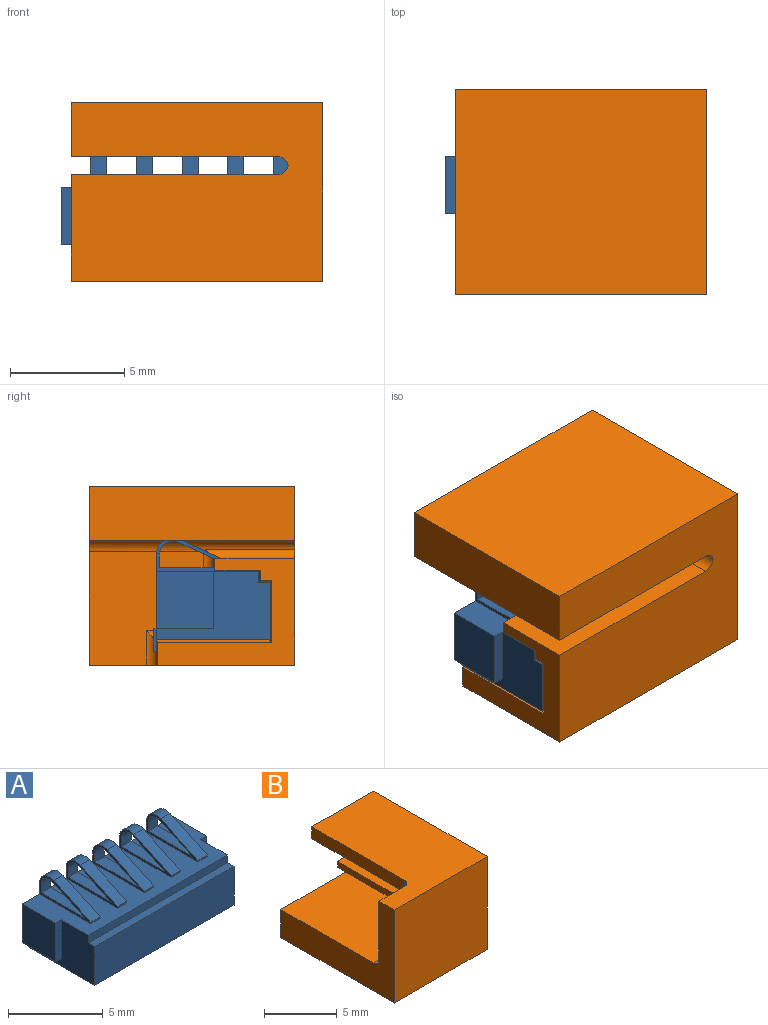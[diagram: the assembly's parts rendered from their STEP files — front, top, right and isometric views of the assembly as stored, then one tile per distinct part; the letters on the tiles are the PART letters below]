
ASSEMBLY  parts=2 mates=1
PART A: 89 faces, bbox 11.3x5.1x5 mm
  f0: plane 11.3x4.5mm, normal (0,0,1), area 35.6mm2, adj f1,f2,f4,f5,f6,f8,f9,f11
  f1: plane 2.5x2.5mm, normal (-1,0,0), area 6.2mm2, adj f0,f4,f5,f12
  f2: plane 2.5x2.5mm, normal (1,0,0), area 6.2mm2, adj f0,f4,f9,f13
  f3: plane 10.4x5mm, normal (0,0,-1), area 52mm2, adj f4,f6,f7,f8,f14,f20,f26,f32
  f4: plane 11.3x3.72mm, normal (0,1,0), area 34.2mm2, adj f0,f1,f2,f3,f6,f8,f12,f13
  f5: plane 2.5x0.45mm, normal (0,-1,0), area 1.1mm2, adj f0,f1,f6,f12
  f6: plane 5x3mm, normal (-1,0,0), area 8.5mm2, adj f0,f3,f4,f5,f7,f10,f11,f12
  f7: plane 10.4x2.5mm, normal (0,-1,0), area 26mm2, adj f3,f6,f8,f10
  f8: plane 5x3mm, normal (1,0,0), area 8.5mm2, adj f0,f3,f4,f7,f9,f10,f11,f13
  f9: plane 2.5x0.45mm, normal (0,-1,0), area 1.1mm2, adj f0,f2,f8,f13
  f10: plane 10.4x0.5mm, normal (0,0,1), area 5.2mm2, adj f6,f7,f8,f11
  f11: plane 10.4x0.5mm, normal (0,-1,0), area 5.2mm2, adj f0,f6,f8,f10
  f12: plane 2.5x0.45mm, normal (0,0,-1), area 1.1mm2, adj f1,f4,f5,f6
  f13: plane 2.5x0.45mm, normal (0,0,-1), area 1.1mm2, adj f2,f4,f8,f9
  f14: plane 0.7x0.5mm, normal (0,-1,0), area 0.4mm2, adj f3,f15,f16,f18
  f15: plane 1x0.13mm, normal (1,0,0), area 0.1mm2, adj f4,f14,f17,f18,f19
  f16: plane 1x0.13mm, normal (-1,0,0), area 0.1mm2, adj f4,f14,f17,f18,f19
  f17: plane 1x0.7mm, normal (0,1,0), area 0.7mm2, adj f15,f16,f18,f19
  f18: plane 0.7x0.13mm, normal (0,0,-1), area 0.1mm2, adj f14,f15,f16,f17
  f19: plane 0.7x0.13mm, normal (0,0,1), area 0.1mm2, adj f4,f15,f16,f17
  f20: plane 0.7x0.5mm, normal (0,-1,0), area 0.4mm2, adj f3,f21,f23,f24
  f21: plane 1x0.13mm, normal (-1,0,0), area 0.1mm2, adj f4,f20,f22,f24,f25
  f22: plane 1x0.7mm, normal (0,1,0), area 0.7mm2, adj f21,f23,f24,f25
  f23: plane 1x0.13mm, normal (1,0,0), area 0.1mm2, adj f4,f20,f22,f24,f25
  f24: plane 0.7x0.13mm, normal (0,0,-1), area 0.1mm2, adj f20,f21,f22,f23
  f25: plane 0.7x0.13mm, normal (0,0,1), area 0.1mm2, adj f4,f21,f22,f23
  f26: plane 0.7x0.5mm, normal (0,-1,0), area 0.4mm2, adj f3,f27,f29,f30
  f27: plane 1x0.13mm, normal (-1,0,0), area 0.1mm2, adj f4,f26,f28,f30,f31
  f28: plane 1x0.7mm, normal (0,1,0), area 0.7mm2, adj f27,f29,f30,f31
  f29: plane 1x0.13mm, normal (1,0,0), area 0.1mm2, adj f4,f26,f28,f30,f31
  f30: plane 0.7x0.13mm, normal (0,0,-1), area 0.1mm2, adj f26,f27,f28,f29
  f31: plane 0.7x0.13mm, normal (0,0,1), area 0.1mm2, adj f4,f27,f28,f29
  f32: plane 0.7x0.5mm, normal (0,-1,0), area 0.4mm2, adj f3,f33,f35,f36
  f33: plane 1x0.13mm, normal (-1,0,0), area 0.1mm2, adj f4,f32,f34,f36,f37
  f34: plane 1x0.7mm, normal (0,1,0), area 0.7mm2, adj f33,f35,f36,f37
  f35: plane 1x0.13mm, normal (1,0,0), area 0.1mm2, adj f4,f32,f34,f36,f37
  f36: plane 0.7x0.13mm, normal (0,0,-1), area 0.1mm2, adj f32,f33,f34,f35
  f37: plane 0.7x0.13mm, normal (0,0,1), area 0.1mm2, adj f4,f33,f34,f35
  f38: plane 0.7x0.5mm, normal (0,-1,0), area 0.3mm2, adj f3,f39,f41,f42
  f39: plane 1x0.13mm, normal (-1,0,0), area 0.1mm2, adj f4,f38,f40,f42,f43
  f40: plane 1x0.7mm, normal (0,1,0), area 0.7mm2, adj f39,f41,f42,f43
  f41: plane 1x0.13mm, normal (1,0,0), area 0.1mm2, adj f4,f38,f40,f42,f43
  f42: plane 0.7x0.13mm, normal (0,0,-1), area 0.1mm2, adj f38,f39,f40,f41
  f43: plane 0.7x0.13mm, normal (0,0,1), area 0.1mm2, adj f4,f39,f40,f41
  f44: plane 3.85x1.47mm, normal (-1,0,0), area 1.3mm2, adj f0,f4,f45,f47,f68,f85,f86,f87
  f45: plane 0.7x0.1mm, normal (0,-1,0), area 0.1mm2, adj f0,f44,f46,f47
  f46: plane 3.85x1.47mm, normal (1,0,0), area 1.3mm2, adj f0,f4,f45,f47,f68,f85,f86,f87
  f47: plane 2.78x1.3mm, normal (0,-0.42,0.91), area 2.1mm2, adj f44,f45,f46,f68
  f48: plane 3.85x1.47mm, normal (-1,0,0), area 1.3mm2, adj f0,f4,f49,f51,f67,f81,f82,f83
  f49: plane 0.7x0.1mm, normal (0,-1,0), area 0.1mm2, adj f0,f48,f50,f51
  f50: plane 3.85x1.47mm, normal (1,0,0), area 1.3mm2, adj f0,f4,f49,f51,f67,f81,f82,f83
  f51: plane 2.78x1.3mm, normal (0,-0.42,0.91), area 2.1mm2, adj f48,f49,f50,f67
  f52: plane 3.85x1.47mm, normal (-1,0,0), area 1.3mm2, adj f0,f4,f53,f55,f66,f77,f78,f79
  f53: plane 0.7x0.1mm, normal (0,-1,0), area 0.1mm2, adj f0,f52,f54,f55
  f54: plane 3.85x1.47mm, normal (1,0,0), area 1.3mm2, adj f0,f4,f53,f55,f66,f77,f78,f79
  f55: plane 2.78x1.3mm, normal (0,-0.42,0.91), area 2.1mm2, adj f52,f53,f54,f66
  f56: plane 3.85x1.47mm, normal (-1,0,0), area 1.3mm2, adj f0,f4,f57,f59,f65,f73,f74,f75
  f57: plane 0.7x0.1mm, normal (0,-1,0), area 0.1mm2, adj f0,f56,f58,f59
  f58: plane 3.85x1.47mm, normal (1,0,0), area 1.3mm2, adj f0,f4,f57,f59,f65,f73,f74,f75
  f59: plane 2.78x1.3mm, normal (0,-0.42,0.91), area 2.1mm2, adj f56,f57,f58,f65
  f60: plane 3.85x1.47mm, normal (-1,0,0), area 1.3mm2, adj f0,f4,f61,f63,f64,f69,f70,f71
  f61: plane 0.7x0.1mm, normal (0,-1,0), area 0.1mm2, adj f0,f60,f62,f63
  f62: plane 3.85x1.47mm, normal (1,0,0), area 1.3mm2, adj f0,f4,f61,f63,f64,f69,f70,f71
  f63: plane 2.78x1.3mm, normal (0,-0.42,0.91), area 2.1mm2, adj f60,f61,f62,f64
  f64: cylinder r=0.75mm len=1.07mm, axis (1,0,0), area 1.1mm2, adj f4,f60,f62,f63
  f65: cylinder r=0.75mm len=1.07mm, axis (1,0,0), area 1.1mm2, adj f4,f56,f58,f59
  f66: cylinder r=0.75mm len=1.07mm, axis (1,0,0), area 1.1mm2, adj f4,f52,f54,f55
  f67: cylinder r=0.75mm len=1.07mm, axis (1,0,0), area 1.1mm2, adj f4,f48,f50,f51
  f68: cylinder r=0.75mm len=1.07mm, axis (1,0,0), area 1.1mm2, adj f4,f44,f46,f47
  f69: plane 3.24x0.7mm, normal (0,0,1), area 2.3mm2, adj f60,f62,f70,f72
  f70: plane 0.7x0.57mm, normal (0,-1,0), area 0.4mm2, adj f60,f62,f69,f71
  f71: cylinder r=0.6mm len=0.85mm, axis (-1,0,0), area 0.8mm2, adj f60,f62,f70,f72
  f72: plane 2.38x1.11mm, normal (0,0.42,-0.91), area 1.8mm2, adj f60,f62,f69,f71
  f73: plane 3.24x0.7mm, normal (0,0,1), area 2.3mm2, adj f56,f58,f74,f76
  f74: plane 0.7x0.57mm, normal (0,-1,0), area 0.4mm2, adj f56,f58,f73,f75
  f75: cylinder r=0.6mm len=0.85mm, axis (-1,0,0), area 0.8mm2, adj f56,f58,f74,f76
  f76: plane 2.38x1.11mm, normal (0,0.42,-0.91), area 1.8mm2, adj f56,f58,f73,f75
  f77: plane 3.24x0.7mm, normal (0,0,1), area 2.3mm2, adj f52,f54,f78,f80
  f78: plane 0.7x0.57mm, normal (0,-1,0), area 0.4mm2, adj f52,f54,f77,f79
  f79: cylinder r=0.6mm len=0.85mm, axis (-1,0,0), area 0.8mm2, adj f52,f54,f78,f80
  f80: plane 2.38x1.11mm, normal (0,0.42,-0.91), area 1.8mm2, adj f52,f54,f77,f79
  f81: plane 3.24x0.7mm, normal (0,0,1), area 2.3mm2, adj f48,f50,f82,f84
  f82: plane 0.7x0.57mm, normal (0,-1,0), area 0.4mm2, adj f48,f50,f81,f83
  f83: cylinder r=0.6mm len=0.85mm, axis (-1,0,0), area 0.8mm2, adj f48,f50,f82,f84
  f84: plane 2.38x1.11mm, normal (0,0.42,-0.91), area 1.8mm2, adj f48,f50,f81,f83
  f85: plane 2.38x1.11mm, normal (0,0.42,-0.91), area 1.8mm2, adj f44,f46,f86,f88
  f86: cylinder r=0.6mm len=0.85mm, axis (-1,0,0), area 0.8mm2, adj f44,f46,f85,f87
  f87: plane 0.7x0.57mm, normal (0,-1,0), area 0.4mm2, adj f44,f46,f86,f88
  f88: plane 3.24x0.7mm, normal (0,0,1), area 2.3mm2, adj f44,f46,f85,f87
PART B: 26 faces, bbox 9x11x7.8 mm
  f0: plane 7.5x4.95mm, normal (0,1,0), area 26.1mm2, adj f10,f13,f18,f19,f20,f21,f22,f23
  f1: plane 9x1mm, normal (-1,0,0), area 9mm2, adj f2,f10,f12,f24
  f2: plane 9x5mm, normal (0,0,-1), area 45mm2, adj f1,f3,f12,f23
  f3: plane 9x2.7mm, normal (-1,0,0), area 24.3mm2, adj f2,f4,f12,f22
  f4: plane 9x0.5mm, normal (0,0,1), area 4.5mm2, adj f3,f5,f12,f21
  f5: plane 9x0.45mm, normal (-1,0,0), area 4mm2, adj f4,f6,f12,f20
  f6: plane 9x2mm, normal (0,0,1), area 18mm2, adj f5,f7,f12,f19
  f7: plane 9x0.5mm, normal (-1,0,0), area 4.5mm2, adj f6,f8,f12,f18
  f8: plane 9x3.5mm, normal (0,0,-1), area 31.5mm2, adj f7,f9,f12,f17
  f9: plane 11x7.8mm, normal (1,0,0), area 78.3mm2, adj f8,f10,f11,f12,f14,f15,f16,f17
  f10: plane 11x9mm, normal (0,0,1), area 70.6mm2, adj f0,f1,f9,f11,f12,f13,f24
  f11: plane 9x7.8mm, normal (0,-1,0), area 70.2mm2, adj f9,f10,f13,f14
  f12: plane 6x4.65mm, normal (0,1,0), area 11.1mm2, adj f1,f2,f3,f4,f5,f6,f7,f8
  f13: plane 11x7.8mm, normal (-1,0,0), area 34mm2, adj f0,f10,f11,f14,f15,f16,f25
  f14: plane 11x9mm, normal (0,0,-1), area 99mm2, adj f9,f11,f13,f15
  f15: plane 9x2.35mm, normal (0,1,0), area 21.1mm2, adj f9,f13,f14,f16
  f16: plane 9x9mm, normal (0,0,1), area 81mm2, adj f9,f13,f15,f25
  f17: cylinder r=0.5mm len=3.9mm, axis (-1,0,0), area 2.5mm2, adj f8,f9,f18,f25
  f18: cylinder r=0.5mm len=1.4mm, axis (0,0,1), area 0.7mm2, adj f0,f7,f17,f19,f25
  f19: cylinder r=0.5mm len=2.5mm, axis (1,0,0), area 1.6mm2, adj f0,f6,f18,f20
  f20: cylinder r=0.5mm len=0.95mm, axis (0,0,1), area 0.4mm2, adj f0,f5,f19,f21
  f21: cylinder r=0.5mm len=1mm, axis (1,0,0), area 0.4mm2, adj f0,f4,f20,f22
  f22: cylinder r=0.5mm len=2.7mm, axis (0,0,1), area 1.8mm2, adj f0,f3,f21,f23
  f23: cylinder r=0.5mm len=5.5mm, axis (-1,0,0), area 3.9mm2, adj f0,f2,f22,f24
  f24: cylinder r=0.5mm len=1.5mm, axis (0,0,1), area 0.9mm2, adj f0,f1,f10,f23
  f25: cylinder r=0.5mm len=9mm, axis (-1,0,0), area 6.7mm2, adj f0,f9,f13,f16,f17,f18
PLACE A t=(-0.29,-3,2.12)mm
PLACE B rot(axis=(0.71,-0.71,0),180deg) t=(-10.69,3.62,-2.54)mm
MATE fastened B.f12 <-> A.f6  axis (-1,0,0) through (-10.69,-3.07,2.02)mm
